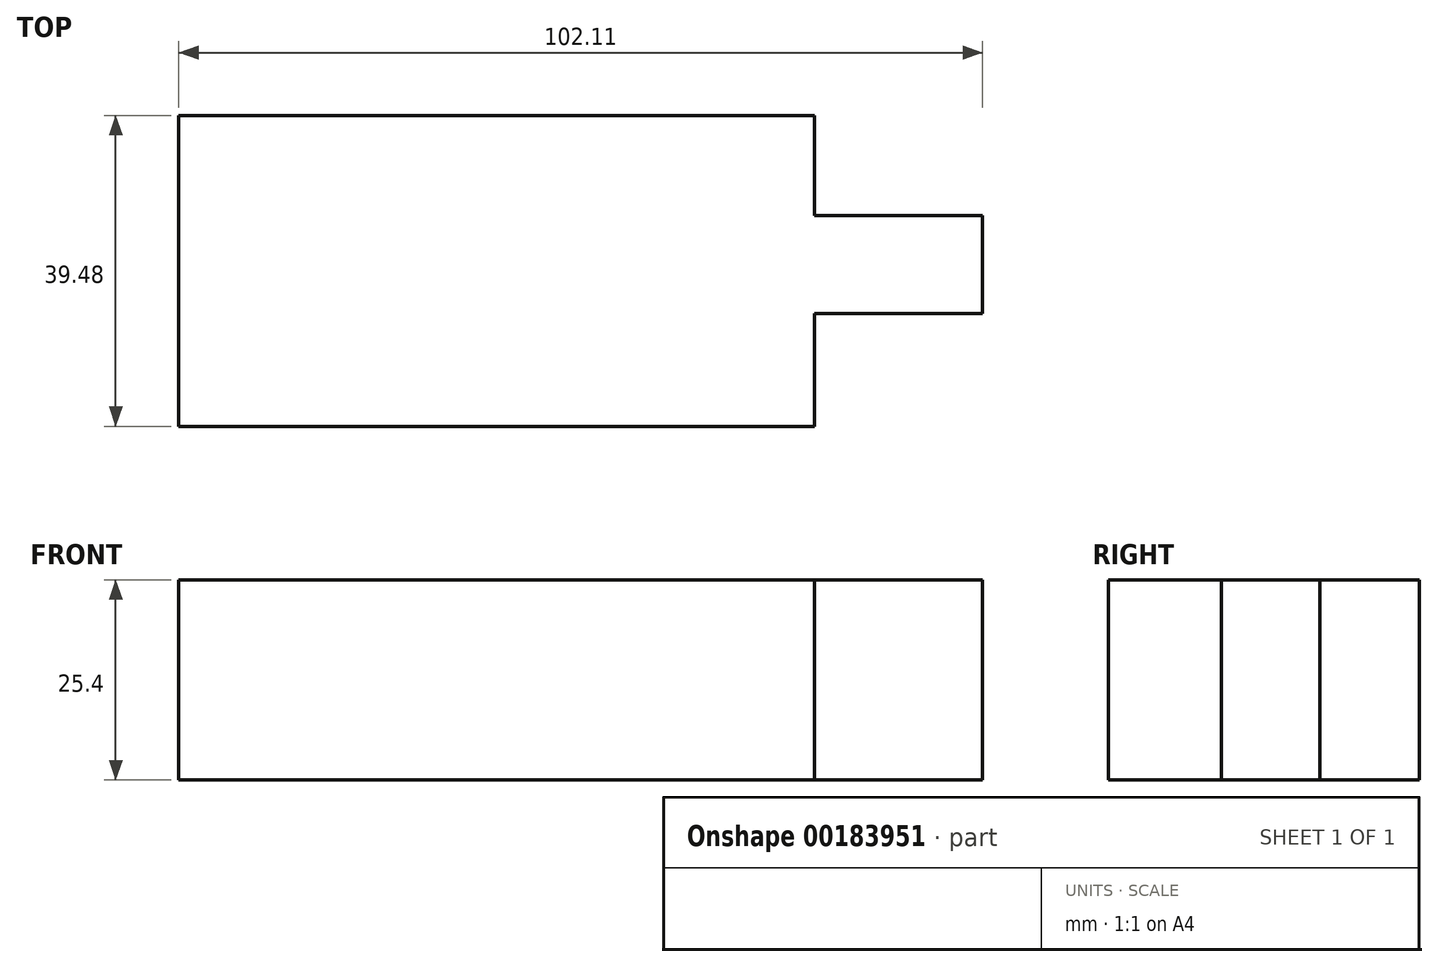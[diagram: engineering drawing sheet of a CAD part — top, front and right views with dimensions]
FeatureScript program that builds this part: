
annotation { "Feature Type Name" : "Feature", "Feature Type Description" : "" }
export const myFeature = defineFeature(function(context is Context, id is Id, definition is map)
    precondition{}
    {
        {
            var Q0;
            Q0=qCreatedBy(makeId("Top.planeOp"),FACE);
            var sketch = newSketch(context, id + "F0", { "sketchPlane" : qUnion([Q0])});
            skLineSegment(sketch, "E0", {"start": v(0, 0) * mm, "end": v(-80.73, 0) * mm});
            skLineSegment(sketch, "E1", {"start": v(-80.73, 0) * mm, "end": v(-80.73, 39.48) * mm});
            skLineSegment(sketch, "E2", {"start": v(-80.73, 39.48) * mm, "end": v(0, 39.48) * mm});
            skLineSegment(sketch, "E3", {"start": v(0, 39.48) * mm, "end": v(0, 26.81) * mm});
            skLineSegment(sketch, "E4", {"start": v(0, 26.81) * mm, "end": v(21.38, 26.81) * mm});
            skLineSegment(sketch, "E5", {"start": v(21.38, 26.81) * mm, "end": v(21.38, 14.36) * mm});
            skLineSegment(sketch, "E6", {"start": v(21.38, 14.36) * mm, "end": v(0, 14.36) * mm});
            skLineSegment(sketch, "E7", {"start": v(0, 14.36) * mm, "end": v(0, 0) * mm});
            skSolve(sketch);
        }
        {
            var Q0;
            Q0 = qSketchRegion(id + "F0", true);
            extrude(context, id + "F1", {"entities" : qUnion([Q0]), "depth" : 25.4 * mm});
        }
    });
